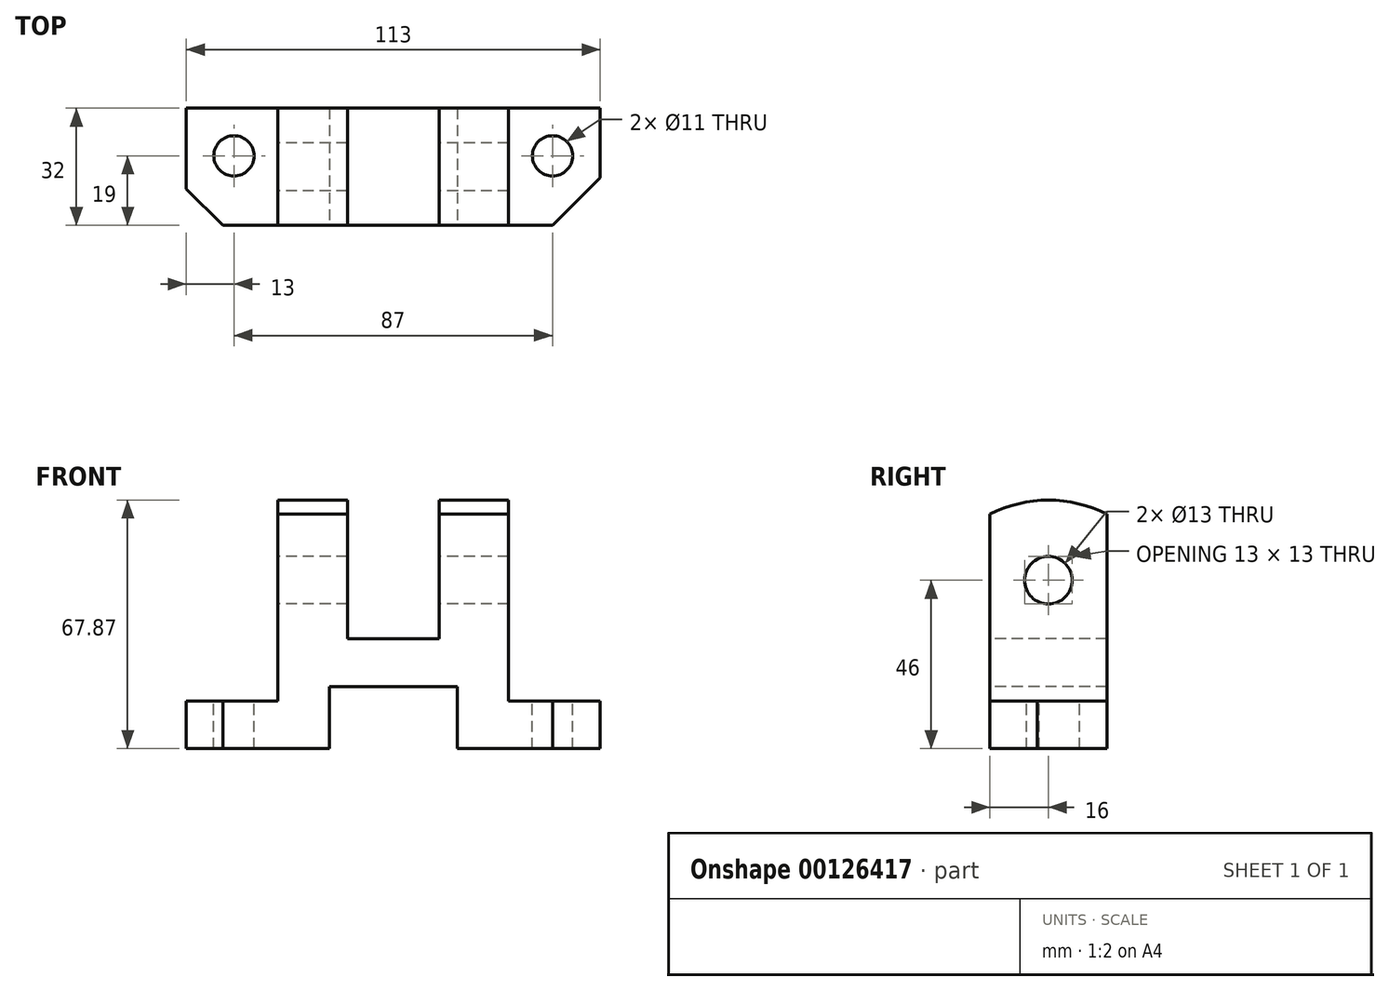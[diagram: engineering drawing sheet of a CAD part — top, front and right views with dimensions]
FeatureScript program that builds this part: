
annotation { "Feature Type Name" : "Feature", "Feature Type Description" : "" }
export const myFeature = defineFeature(function(context is Context, id is Id, definition is map)
    precondition{}
    {
        {
            var Q0;
            Q0=qCreatedBy(makeId("Front.planeOp"),FACE);
            var sketch = newSketch(context, id + "F0", { "sketchPlane" : qUnion([Q0])});
            skLineSegment(sketch, "E0", {"start": v(0, 0) * mm, "end": v(39, 0) * mm});
            skLineSegment(sketch, "E1", {"start": v(74, 0) * mm, "end": v(113, 0) * mm});
            skLineSegment(sketch, "E2", {"start": v(113, 0) * mm, "end": v(113, 13) * mm});
            skLineSegment(sketch, "E3", {"start": v(113, 13) * mm, "end": v(88, 13) * mm});
            skLineSegment(sketch, "E4", {"start": v(88, 13) * mm, "end": v(88, 64) * mm});
            skLineSegment(sketch, "E5", {"start": v(44, 30) * mm, "end": v(44, 64) * mm});
            skLineSegment(sketch, "E6", {"start": v(44, 64) * mm, "end": v(25, 64) * mm});
            skLineSegment(sketch, "E7", {"start": v(25, 64) * mm, "end": v(25, 13) * mm});
            skLineSegment(sketch, "E8", {"start": v(25, 13) * mm, "end": v(0, 13) * mm});
            skLineSegment(sketch, "E9", {"start": v(0, 13) * mm, "end": v(0, 0) * mm});
            skLineSegment(sketch, "E10", {"start": v(88, 64) * mm, "end": v(69, 64) * mm});
            skLineSegment(sketch, "E11", {"start": v(69, 64) * mm, "end": v(69, 30) * mm});
            skLineSegment(sketch, "E12", {"start": v(69, 30) * mm, "end": v(44, 30) * mm});
            skLineSegment(sketch, "E13", {"start": v(39, 0) * mm, "end": v(39, 17) * mm});
            skLineSegment(sketch, "E14", {"start": v(39, 17) * mm, "end": v(74, 17) * mm});
            skLineSegment(sketch, "E15", {"start": v(74, 17) * mm, "end": v(74, 0) * mm});
            skSolve(sketch);
        }
        {
            var Q0;
            Q0=makeQuery(id+"F0.imprint","IMPRINT",FACE,{"disambiguationData":[TD([[makeQuery(id+"F0.imprint","IMPRINT",EDGE,{"derivedFrom":sQuery(id+"F0.wireOp",EDGE,"E0")}),1.0]])]});
            extrude(context, id + "F1", {"entities" : qUnion([Q0]), "oppositeDirection" : true, "depth" : 32 * mm});
        }
        {
            var Q0;
            Q0=makeQuery(id+"F1.opExtrude","CAP_EDGE",EDGE,{"disambiguationData":[OSD([sQuery(id+"F0.wireOp",EDGE,"E9")])],"isStart":true});
            chamfer(context, id + "F2", {"entities" : qUnion([Q0]), "width" : 10 * mm, "tangentPropagation" : true});
        }
        {
            var Q0;
            Q0=makeQuery(id+"F1.opExtrude","CAP_EDGE",EDGE,{"disambiguationData":[OSD([sQuery(id+"F0.wireOp",EDGE,"E2")])],"isStart":true});
            chamfer(context, id + "F3", {"entities" : qUnion([Q0]), "width" : 13 * mm, "tangentPropagation" : true});
        }
        {
            var Q0;
            Q0=makeQuery(id+"F1.opExtrude","SWEPT_FACE",FACE,{"disambiguationData":[OSD([sQuery(id+"F0.wireOp",EDGE,"E8")])]});
            var sketch = newSketch(context, id + "F4", { "sketchPlane" : qUnion([Q0])});
            skLineSegment(sketch, "E16", {"start": v(0, 32) * mm, "end": v(13, 32) * mm, "construction": true});
            skLineSegment(sketch, "E17", {"start": v(13, 32) * mm, "end": v(13, 19) * mm, "construction": true});
            skCircle(sketch, "E18", {"center": v(13, 19) * mm, "radius": 5.5 * mm});
            skSolve(sketch);
        }
        {
            var Q0;
            Q0=makeQuery(id+"F1.opExtrude","SWEPT_FACE",FACE,{"disambiguationData":[OSD([sQuery(id+"F0.wireOp",EDGE,"E3")])]});
            var sketch = newSketch(context, id + "F5", { "sketchPlane" : qUnion([Q0])});
            skLineSegment(sketch, "E19", {"start": v(113, 32) * mm, "end": v(100, 32) * mm, "construction": true});
            skLineSegment(sketch, "E20", {"start": v(100, 32) * mm, "end": v(100, 19) * mm, "construction": true});
            skCircle(sketch, "E21", {"center": v(100, 19) * mm, "radius": 5.5 * mm});
            skSolve(sketch);
        }
        {
            var Q0;
            Q0=makeQuery(id+"F4.imprint","IMPRINT",FACE,{"disambiguationData":[TD([[makeQuery(id+"F4.imprint","IMPRINT",EDGE,{"derivedFrom":sQuery(id+"F4.wireOp",EDGE,"E18")}),1.0]])]});
            var Q1;
            Q1=makeQuery(id+"F5.imprint","IMPRINT",FACE,{"disambiguationData":[TD([[makeQuery(id+"F5.imprint","IMPRINT",EDGE,{"derivedFrom":sQuery(id+"F5.wireOp",EDGE,"E21")}),1.0]])]});
            extrude(context, id + "F6", {"entities" : qUnion([Q0, Q1]), "operationType" : NewBodyOperationType.REMOVE, "oppositeDirection" : true, "depth" : 25 * mm});
        }
        {
            var Q0;
            Q0=makeQuery(id+"F1.opExtrude","SWEPT_FACE",FACE,{"disambiguationData":[OSD([sQuery(id+"F0.wireOp",EDGE,"E7")])]});
            var sketch = newSketch(context, id + "F7", { "sketchPlane" : qUnion([Q0])});
            skLineSegment(sketch, "E22", {"start": v(0, 0) * mm, "end": v(0, 46) * mm, "construction": true});
            skLineSegment(sketch, "E23", {"start": v(0, 46) * mm, "end": v(-16, 46) * mm, "construction": true});
            skPoint(sketch, "E23.endSnap0", {"position": v(-16, 64) * mm});
            skCircle(sketch, "E24", {"center": v(-16, 46) * mm, "radius": 6.5 * mm});
            skSolve(sketch);
        }
        {
            var Q0;
            Q0=makeQuery(id+"F7.imprint","IMPRINT",FACE,{"disambiguationData":[TD([[makeQuery(id+"F7.imprint","IMPRINT",EDGE,{"derivedFrom":sQuery(id+"F7.wireOp",EDGE,"E24")}),1.0]])]});
            extrude(context, id + "F8", {"entities" : qUnion([Q0]), "operationType" : NewBodyOperationType.REMOVE, "oppositeDirection" : true, "depth" : 100 * mm});
        }
        {
            var Q0;
            Q0=makeQuery(id+"F1.opExtrude","SWEPT_FACE",FACE,{"disambiguationData":[OSD([sQuery(id+"F0.wireOp",EDGE,"E6")])]});
            var Q1;
            Q1=makeQuery(id+"F1.opExtrude","SWEPT_FACE",FACE,{"disambiguationData":[OSD([sQuery(id+"F0.wireOp",EDGE,"E10")])]});
            extrude(context, id + "F9", {"entities" : qUnion([Q0, Q1]), "operationType" : NewBodyOperationType.REMOVE, "oppositeDirection" : true, "depth" : (64 - 46) * mm});
        }
        {
            var Q0;
            Q0=makeQuery(id+"F1.opExtrude","SWEPT_FACE",FACE,{"disambiguationData":[OSD([sQuery(id+"F0.wireOp",EDGE,"E4")])]});
            var sketch = newSketch(context, id + "F10", { "sketchPlane" : qUnion([Q0])});
            skLineSegment(sketch, "E25", {"start": v(0, 46) * mm, "end": v(0, 64) * mm});
            skLineSegment(sketch, "E26", {"start": v(32, 46) * mm, "end": v(32, 64) * mm});
            skPoint(sketch, "E27.startSnap0", {"position": v(16, 39.5) * mm});
            skArc(sketch, "E28", {"start": v(0, 64) * mm, "mid": v(16, 67.87) * mm, "end": v(32, 64) * mm});
            skCircle(sketch, "E29", {"center": v(16, 46) * mm, "radius": 6.5 * mm});
            skSolve(sketch);
        }
        {
            var Q0;
            Q0=makeQuery(id+"F10.imprint","IMPRINT",FACE,{"disambiguationData":[TD([[makeQuery(id+"F10.imprint","IMPRINT",EDGE,{"derivedFrom":sQuery(id+"F10.wireOp",EDGE,"E25")}),-1.0]])]});
            extrude(context, id + "F11", {"entities" : qUnion([Q0]), "operationType" : NewBodyOperationType.ADD, "oppositeDirection" : true, "depth" : (19 + 25 + 19) * mm});
        }
        {
            var Q0;
            Q0=makeQuery(id+"F1.opExtrude","SWEPT_FACE",FACE,{"disambiguationData":[OSD([sQuery(id+"F0.wireOp",EDGE,"E12")])]});
            extrude(context, id + "F12", {"entities" : qUnion([Q0]), "operationType" : NewBodyOperationType.REMOVE, "depth" : 64.45 * mm});
        }
    });
